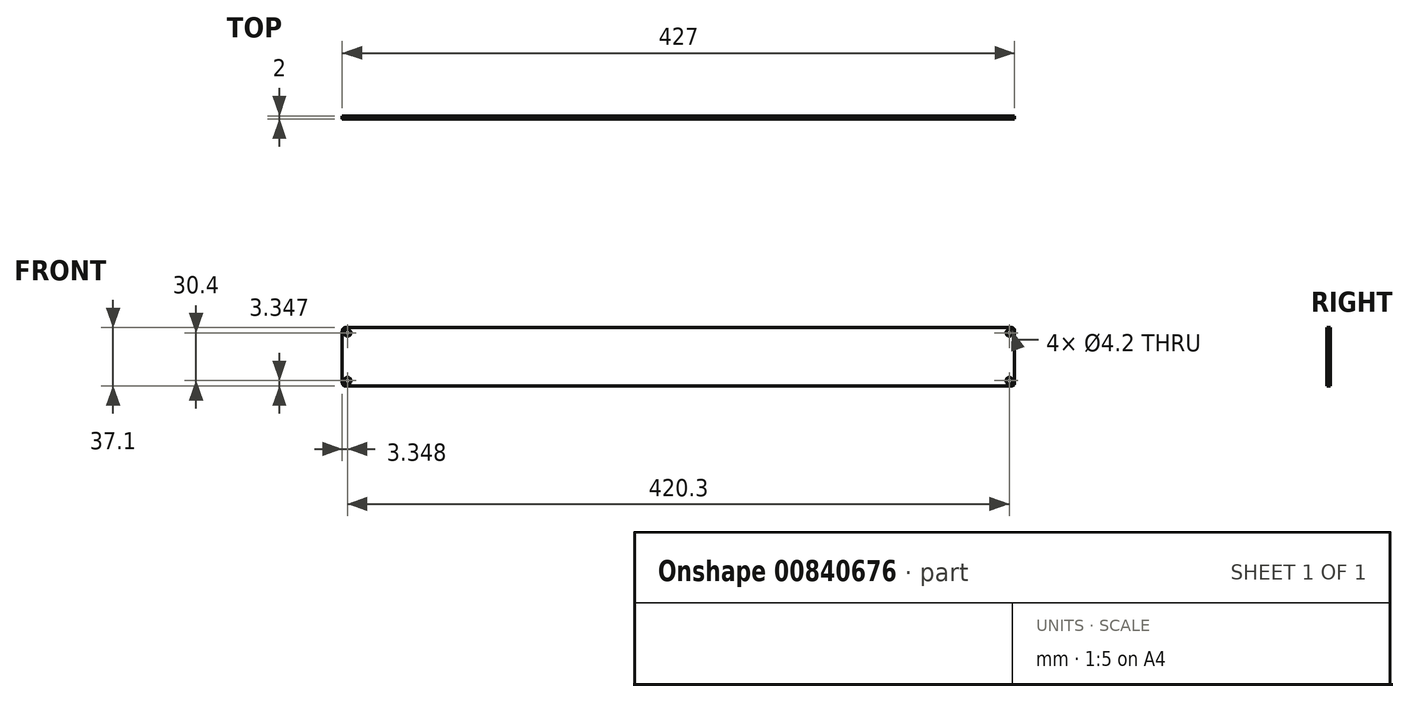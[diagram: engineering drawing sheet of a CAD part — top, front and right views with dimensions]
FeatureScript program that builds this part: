
annotation { "Feature Type Name" : "Feature", "Feature Type Description" : "" }
export const myFeature = defineFeature(function(context is Context, id is Id, definition is map)
    precondition{}
    {
        {
            var Q0;
            Q0=qCreatedBy(makeId("Front.planeOp"),FACE);
            var sketch = newSketch(context, id + "F0", { "sketchPlane" : qUnion([Q0])});
            skLineSegment(sketch, "E0.bottom", {"start": v(-214.73, -20.25) * mm, "end": v(212.27, -20.25) * mm});
            skLineSegment(sketch, "E0.top", {"start": v(-214.73, -57.35) * mm, "end": v(212.27, -57.35) * mm});
            skLineSegment(sketch, "E0.left", {"start": v(-214.73, -20.25) * mm, "end": v(-214.73, -57.35) * mm});
            skLineSegment(sketch, "E0.right", {"start": v(212.27, -20.25) * mm, "end": v(212.27, -57.35) * mm});
            skSolve(sketch);
        }
        {
            var Q0;
            Q0=makeQuery(id+"F0.imprint","IMPRINT",FACE,{"disambiguationData":[TD([[makeQuery(id+"F0.imprint","IMPRINT",EDGE,{"derivedFrom":sQuery(id+"F0.wireOp",EDGE,"E0.bottom")}),-1.0]])]});
            extrude(context, id + "F1", {"entities" : qUnion([Q0]), "depth" : 2 * mm, "offsetDistance" : 25 * mm});
        }
        {
            var Q0;
            Q0=makeQuery(id+"F1.opExtrude","SWEPT_EDGE",EDGE,{"disambiguationData":[OSD([sQuery(id+"F0.wireOp",EDGE,"E0.bottom"),sQuery(id+"F0.wireOp",EDGE,"E0.left")])]});
            var Q1;
            Q1=makeQuery(id+"F1.opExtrude","SWEPT_EDGE",EDGE,{"disambiguationData":[OSD([sQuery(id+"F0.wireOp",EDGE,"E0.top"),sQuery(id+"F0.wireOp",EDGE,"E0.left")])]});
            var Q2;
            Q2=makeQuery(id+"F1.opExtrude","SWEPT_EDGE",EDGE,{"disambiguationData":[OSD([sQuery(id+"F0.wireOp",EDGE,"E0.top"),sQuery(id+"F0.wireOp",EDGE,"E0.right")])]});
            var Q3;
            Q3=makeQuery(id+"F1.opExtrude","SWEPT_EDGE",EDGE,{"disambiguationData":[OSD([sQuery(id+"F0.wireOp",EDGE,"E0.bottom"),sQuery(id+"F0.wireOp",EDGE,"E0.right")])]});
            fillet(context, id + "F2", {"entities" : qUnion([Q0, Q1, Q2, Q3]), "radius" : 2.02 * mm, "tangentPropagation" : true, "allowEdgeOverflow" : false});
        }
        {
            var Q0;
            Q0=makeQuery(id+"F1.opExtrude","CAP_FACE",FACE,{"disambiguationData":[OSD([sQuery(id+"F0.wireOp",EDGE,"E0.bottom"),sQuery(id+"F0.wireOp",EDGE,"E0.top"),sQuery(id+"F0.wireOp",EDGE,"E0.left"),sQuery(id+"F0.wireOp",EDGE,"E0.right")])],"isStart":false});
            var sketch = newSketch(context, id + "F3", { "sketchPlane" : qUnion([Q0])});
            skCircle(sketch, "E1", {"center": v(-211.38, -23.6) * mm, "radius": 2.1 * mm});
            skSolve(sketch);
        }
        {
            var Q0;
            Q0=makeQuery(id+"F3.imprint","IMPRINT",FACE,{"disambiguationData":[TD([[makeQuery(id+"F3.imprint","IMPRINT",EDGE,{"derivedFrom":sQuery(id+"F3.wireOp",EDGE,"E1")}),-1.0]])]});
            var sketch = newSketch(context, id + "F4", { "sketchPlane" : qUnion([Q0])});
            skCircle(sketch, "E2", {"center": v(-211.38, -54) * mm, "radius": 2.1 * mm});
            skSolve(sketch);
        }
        {
            var Q0;
            Q0=makeQuery(id+"F3.imprint","IMPRINT",FACE,{"disambiguationData":[TD([[makeQuery(id+"F3.imprint","IMPRINT",EDGE,{"derivedFrom":sQuery(id+"F3.wireOp",EDGE,"E1")}),-1.0]])]});
            var sketch = newSketch(context, id + "F5", { "sketchPlane" : qUnion([Q0])});
            skCircle(sketch, "E3", {"center": v(208.92, -23.6) * mm, "radius": 2.1 * mm});
            skCircle(sketch, "E4", {"center": v(208.92, -54) * mm, "radius": 2.1 * mm});
            skSolve(sketch);
        }
        {
            var Q0;
            Q0=makeQuery(id+"F3.imprint","IMPRINT",FACE,{"disambiguationData":[TD([[makeQuery(id+"F3.imprint","IMPRINT",EDGE,{"derivedFrom":sQuery(id+"F3.wireOp",EDGE,"E1")}),1.0]])]});
            extrude(context, id + "F6", {"entities" : qUnion([Q0]), "operationType" : NewBodyOperationType.REMOVE, "oppositeDirection" : true, "depth" : 25 * mm, "offsetDistance" : 25 * mm});
        }
        {
            var Q0;
            Q0=makeQuery(id+"F4.imprint","IMPRINT",FACE,{"disambiguationData":[TD([[makeQuery(id+"F4.imprint","IMPRINT",EDGE,{"derivedFrom":sQuery(id+"F4.wireOp",EDGE,"E2")}),1.0]])]});
            var Q1;
            Q1=makeQuery(id+"F5.imprint","IMPRINT",FACE,{"disambiguationData":[TD([[makeQuery(id+"F5.imprint","IMPRINT",EDGE,{"derivedFrom":sQuery(id+"F5.wireOp",EDGE,"E3")}),1.0]])]});
            var Q2;
            Q2=makeQuery(id+"F5.imprint","IMPRINT",FACE,{"disambiguationData":[TD([[makeQuery(id+"F5.imprint","IMPRINT",EDGE,{"derivedFrom":sQuery(id+"F5.wireOp",EDGE,"E4")}),1.0]])]});
            extrude(context, id + "F7", {"entities" : qUnion([Q0, Q1, Q2]), "operationType" : NewBodyOperationType.REMOVE, "oppositeDirection" : true, "depth" : 25 * mm, "offsetDistance" : 25 * mm});
        }
    });
